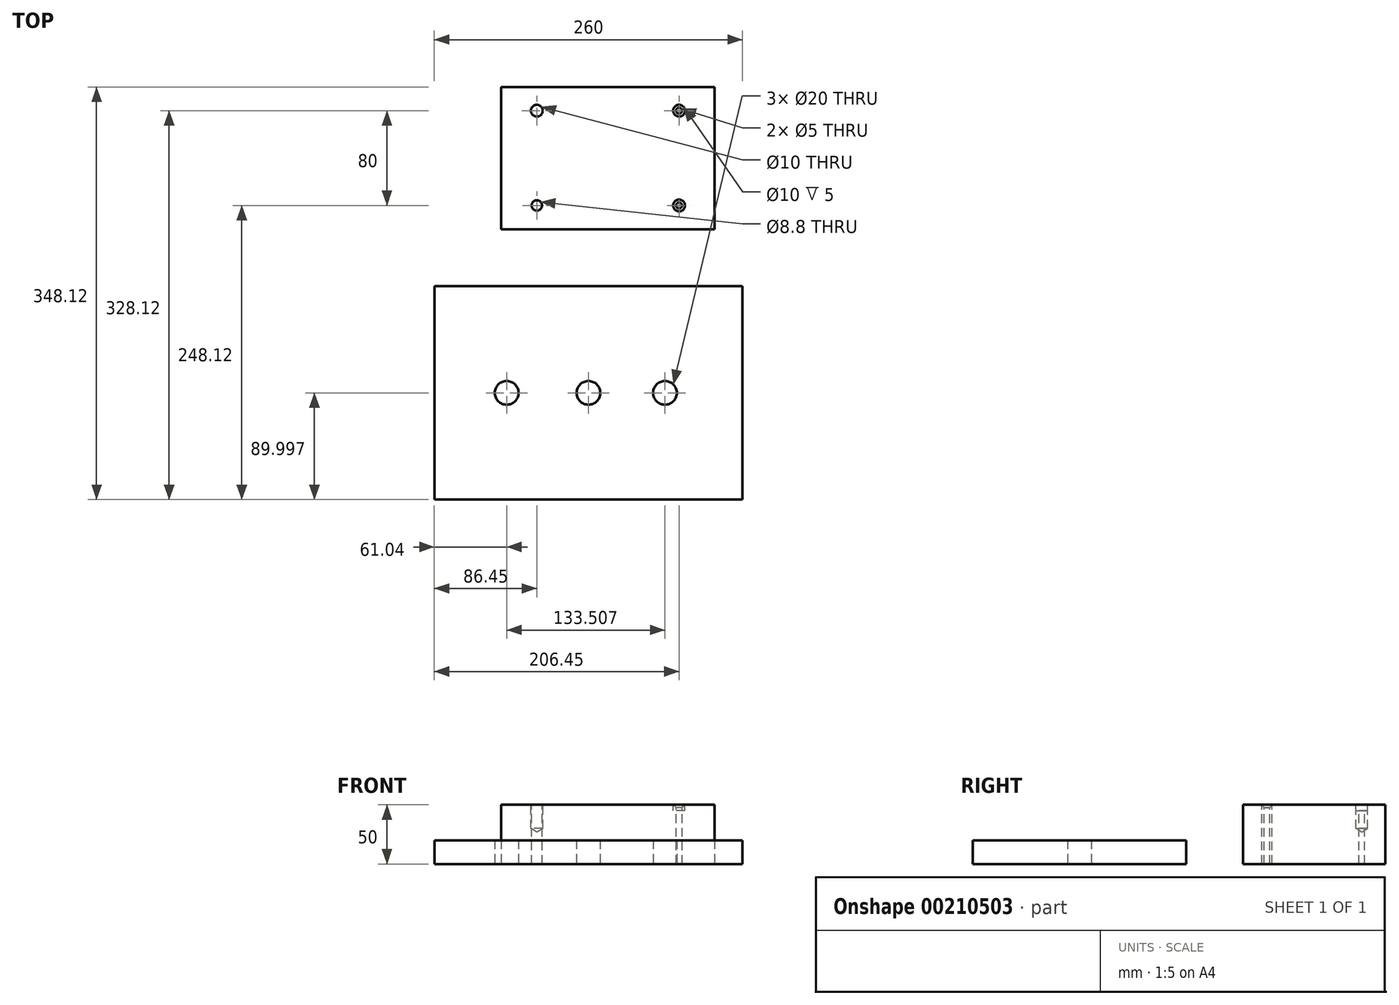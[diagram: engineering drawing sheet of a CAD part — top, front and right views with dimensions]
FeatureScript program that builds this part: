
annotation { "Feature Type Name" : "Feature", "Feature Type Description" : "" }
export const myFeature = defineFeature(function(context is Context, id is Id, definition is map)
    precondition{}
    {
        {
            var Q0;
            Q0=qCreatedBy(makeId("Top.planeOp"),FACE);
            var sketch = newSketch(context, id + "F0", { "sketchPlane" : qUnion([Q0])});
            skLineSegment(sketch, "E0.rect.bottom", {"start": v(-90, 60) * mm, "end": v(90, 60) * mm});
            skLineSegment(sketch, "E0.rect.top", {"start": v(-90, -60) * mm, "end": v(90, -60) * mm});
            skLineSegment(sketch, "E0.rect.left", {"start": v(-90, 60) * mm, "end": v(-90, -60) * mm});
            skLineSegment(sketch, "E0.rect.right", {"start": v(90, 60) * mm, "end": v(90, -60) * mm});
            skPoint(sketch, "E0.rect.middle", {"position": v(0, 0) * mm});
            skSolve(sketch);
        }
        {
            var Q0;
            Q0=qSketchRegion(id+"F0",true);
            extrude(context, id + "F1", {"entities" : qUnion([Q0]), "depth" : 50 * mm});
        }
        {
            var Q0;
            Q0=makeQuery(id+"F1.opExtrude","CAP_FACE",FACE,{"disambiguationData":[OSD([sQuery(id+"F0.wireOp",EDGE,"E0.rect.bottom"),sQuery(id+"F0.wireOp",EDGE,"E0.rect.top"),sQuery(id+"F0.wireOp",EDGE,"E0.rect.left"),sQuery(id+"F0.wireOp",EDGE,"E0.rect.right")])],"isStart":false});
            var sketch = newSketch(context, id + "F2", { "sketchPlane" : qUnion([Q0])});
            skLineSegment(sketch, "E1.rect.bottom", {"start": v(-60, 40) * mm, "end": v(60, 40) * mm});
            skLineSegment(sketch, "E1.rect.top", {"start": v(-60, -40) * mm, "end": v(60, -40) * mm});
            skLineSegment(sketch, "E1.rect.left", {"start": v(-60, 40) * mm, "end": v(-60, -40) * mm});
            skLineSegment(sketch, "E1.rect.right", {"start": v(60, 40) * mm, "end": v(60, -40) * mm});
            skPoint(sketch, "E1.rect.middle", {"position": v(0, 0) * mm});
            skSolve(sketch);
        }
        {
            var Q0;
            Q0=sQuery(id+"F2.wireOp",VERTEX,"E1.rect.left.start");
            var Q1;
            Q1=makeQuery(id+"F1.opExtrude","SWEPT_BODY",BODY,{"disambiguationData":[OSD([sQuery(id+"F0.wireOp",EDGE,"E0.rect.bottom"),sQuery(id+"F0.wireOp",EDGE,"E0.rect.top"),sQuery(id+"F0.wireOp",EDGE,"E0.rect.left"),sQuery(id+"F0.wireOp",EDGE,"E0.rect.right")])]});
            hole(context, id + "F3", {"style" : HoleStyle.SIMPLE, "holeDiameter" : 10 * mm, "endStyle" : HoleEndStyle.BLIND, "holeDepth" : 20 * mm, "locations" : qUnion([Q0]), "scope" : qUnion([Q1])});
        }
        {
            var Q0;
            Q0=sQuery(id+"F2.wireOp",VERTEX,"E1.rect.right.start");
            var Q1;
            Q1=makeQuery(id+"F1.opExtrude","SWEPT_BODY",BODY,{"disambiguationData":[OSD([sQuery(id+"F0.wireOp",EDGE,"E0.rect.bottom"),sQuery(id+"F0.wireOp",EDGE,"E0.rect.top"),sQuery(id+"F0.wireOp",EDGE,"E0.rect.left"),sQuery(id+"F0.wireOp",EDGE,"E0.rect.right")])]});
            hole(context, id + "F4", {"style" : HoleStyle.C_BORE, "holeDiameter" : 5 * mm, "cBoreDiameter" : 10 * mm, "cBoreDepth" : 5 * mm, "endStyle" : HoleEndStyle.THROUGH, "locations" : qUnion([Q0]), "scope" : qUnion([Q1])});
        }
        {
            var Q0;
            Q0=sQuery(id+"F2.wireOp",VERTEX,"E1.rect.top.end");
            var Q1;
            Q1=makeQuery(id+"F1.opExtrude","SWEPT_BODY",BODY,{"disambiguationData":[OSD([sQuery(id+"F0.wireOp",EDGE,"E0.rect.bottom"),sQuery(id+"F0.wireOp",EDGE,"E0.rect.top"),sQuery(id+"F0.wireOp",EDGE,"E0.rect.left"),sQuery(id+"F0.wireOp",EDGE,"E0.rect.right")])]});
            hole(context, id + "F5", {"style" : HoleStyle.C_SINK, "holeDiameter" : 5 * mm, "cSinkDiameter" : 10 * mm, "endStyle" : HoleEndStyle.THROUGH, "locations" : qUnion([Q0]), "scope" : qUnion([Q1]), "cSinkAngle" : 90 * degree});
        }
        {
            var Q0;
            Q0=qCreatedBy(makeId("Top.planeOp"),FACE);
            var sketch = newSketch(context, id + "F6", { "sketchPlane" : qUnion([Q0])});
            skLineSegment(sketch, "E2", {"start": v(123.55, -298.12) * mm, "end": v(-156.45, -298.12) * mm});
            skLineSegment(sketch, "E3", {"start": v(113.55, -288.12) * mm, "end": v(113.55, -108.12) * mm});
            skLineSegment(sketch, "E4", {"start": v(113.55, -108.12) * mm, "end": v(-146.45, -108.12) * mm});
            skLineSegment(sketch, "E5", {"start": v(-146.45, -108.12) * mm, "end": v(-146.45, -288.12) * mm});
            skLineSegment(sketch, "E6", {"start": v(-146.45, -288.12) * mm, "end": v(113.55, -288.12) * mm});
            skLineSegment(sketch, "E7", {"start": v(-156.45, -298.12) * mm, "end": v(-156.45, -98.12) * mm});
            skLineSegment(sketch, "E8", {"start": v(-156.45, -98.12) * mm, "end": v(123.55, -98.12) * mm});
            skLineSegment(sketch, "E9", {"start": v(123.55, -98.12) * mm, "end": v(123.55, -298.12) * mm});
            skLineSegment(sketch, "E10", {"start": v(123.55, -98.12) * mm, "end": v(113.55, -108.12) * mm});
            skLineSegment(sketch, "E11", {"start": v(-146.45, -108.12) * mm, "end": v(-156.45, -98.12) * mm});
            skLineSegment(sketch, "E12", {"start": v(123.55, -298.12) * mm, "end": v(113.55, -288.12) * mm});
            skLineSegment(sketch, "E13", {"start": v(-146.45, -288.12) * mm, "end": v(-156.45, -298.12) * mm});
            skCircle(sketch, "E14", {"center": v(-85.4, -198.12) * mm, "radius": 10 * mm});
            skCircle(sketch, "E15", {"center": v(-16.45, -198.12) * mm, "radius": 10 * mm});
            skCircle(sketch, "E16", {"center": v(48.1, -198.12) * mm, "radius": 10 * mm});
            skSolve(sketch);
        }
        {
            var Q0;
            Q0=makeQuery(id+"F6.imprint","IMPRINT",FACE,{"disambiguationData":[TD([[makeQuery(id+"F6.imprint","IMPRINT",EDGE,{"derivedFrom":sQuery(id+"F6.wireOp",EDGE,"E3")}),1.0]])]});
            extrude(context, id + "F7", {"entities" : qUnion([Q0]), "depth" : 20 * mm});
        }
        {
            var Q0;
            Q0=sQuery(id+"F2.wireOp",VERTEX,"E1.rect.left.end");
            var Q1;
            Q1=makeQuery(id+"F1.opExtrude","SWEPT_BODY",BODY,{"disambiguationData":[OSD([sQuery(id+"F0.wireOp",EDGE,"E0.rect.bottom"),sQuery(id+"F0.wireOp",EDGE,"E0.rect.top"),sQuery(id+"F0.wireOp",EDGE,"E0.rect.left"),sQuery(id+"F0.wireOp",EDGE,"E0.rect.right")])]});
            hole(context, id + "F8", {"style" : HoleStyle.SIMPLE, "endStyle" : HoleEndStyle.THROUGH, "standardTappedOrClearance" : lookupTablePath({ "standard" : "ISO", "engagement" : "75%", "pitch" : "1.25 mm", "size" : "M10", "type" : "Tapped" }), "standardBlindInLast" : lookupTablePath({ "standard" : "ISO", "engagement" : "75%", "pitch" : "1.25 mm", "size" : "M10", "type" : "Tapped" }), "holeDiameter" : 8.8 * mm, "startFromSketch" : true, "locations" : qUnion([Q0]), "scope" : qUnion([Q1]), "isTappedThrough" : true, "majorDiameter" : 10 * mm, "showTappedDepth" : true});
        }
    });
